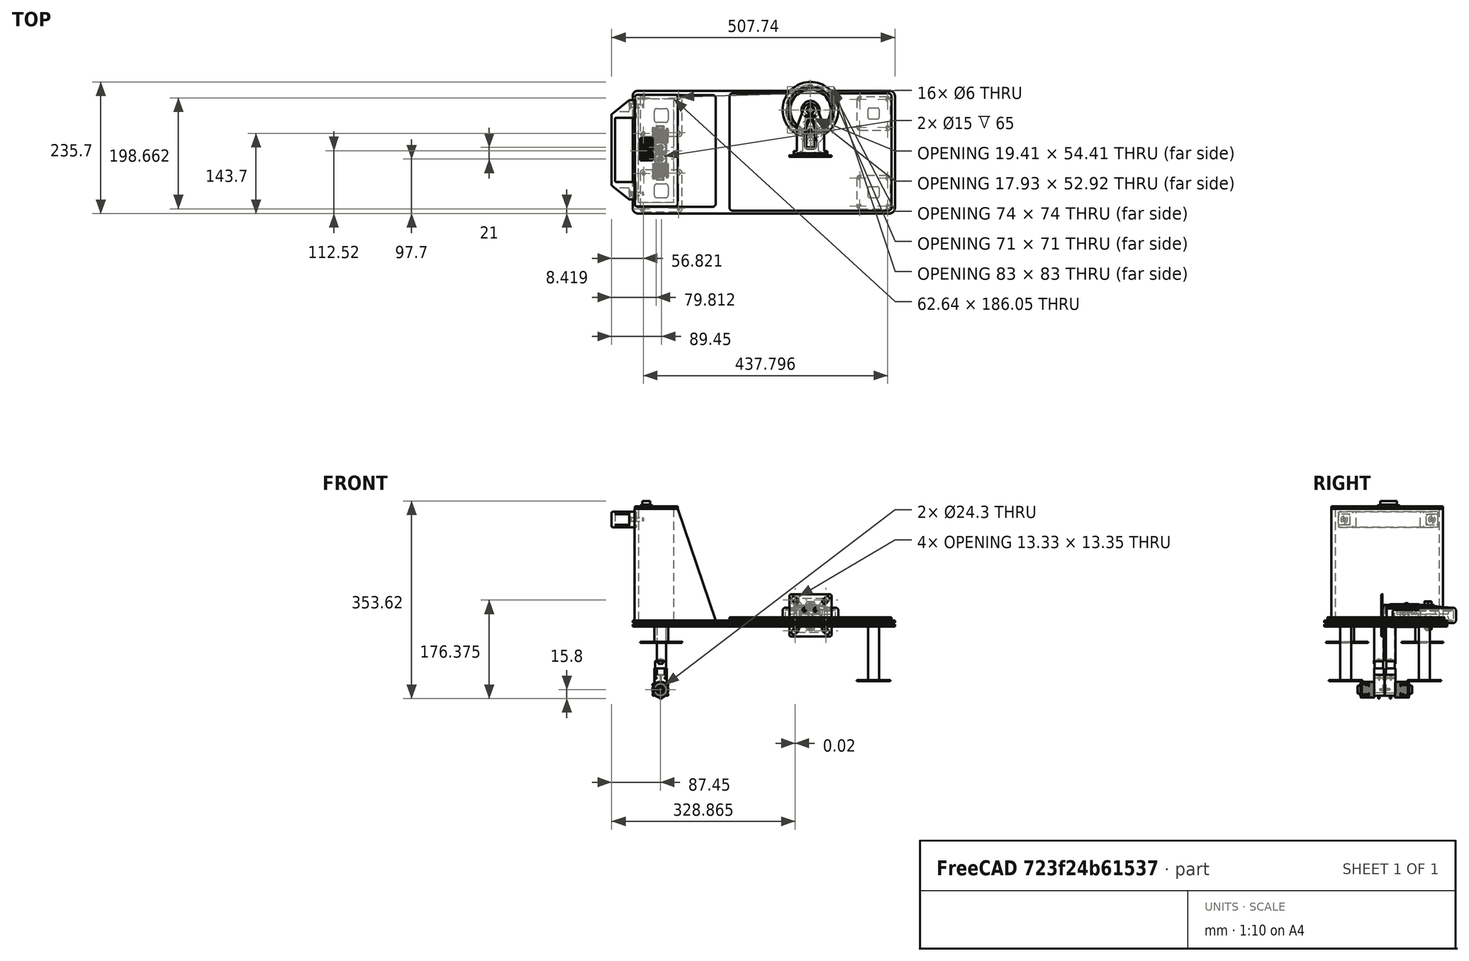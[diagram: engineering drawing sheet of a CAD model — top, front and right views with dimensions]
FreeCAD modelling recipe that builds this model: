
FCSTD DOCUMENT  (FreeCAD 0.19R24267 (Git))
Label: Assembly
License: All rights reserved
LicenseURL: http://en.wikipedia.org/wiki/All_rights_reserved
objects: PartDesign::Fillet×53, Part::Feature×42, Sketcher::SketchObject×24, PartDesign::Pad×15, PartDesign::Hole×12, PartDesign::Body×11, Part::Compound2×4, PartDesign::Pocket×3, Mesh::Feature×1
note: 243 computed .brp shape members not serialized (recipe doc carries the construction recipe); baked Part::Feature solids carry a one-line shape summary decoded from their .brp

FEATURE [Part::Feature] Solid004
  shape: bbox 35.72 x 35.72 x 6.7 mm, 21 faces (baked)
FEATURE [Part::Feature] Solid003
  shape: bbox 35.72 x 35.72 x 6.7 mm, 21 faces (baked)
FEATURE [Part::Feature] Solid
  shape: bbox 44.32 x 44.32 x 22 mm, 34 faces (baked)
FEATURE [Part::Feature] Solid002
  shape: bbox 8 x 8 x 23 mm, 6 faces (baked)
FEATURE [Part::Feature] Solid008
  shape: bbox 42.23 x 52 x 29.25 mm, 248 faces (baked)
FEATURE [Part::Feature] Solid001
  shape: bbox 53.41 x 53.41 x 20 mm, 10 faces (baked)
FEATURE [Part::Feature] Solid007
  shape: bbox 11.32 x 11.32 x 6 mm, 21 faces (baked)
FEATURE [Part::Feature] Solid006
  shape: bbox 12.03 x 11.6 x 41.03 mm, 57 faces (baked)
FEATURE [Part::Feature] Solid005
  shape: bbox 60 x 5.2 x 60 mm, 62 faces (baked)
FEATURE [Part::Compound2] Compound  label="Castor 50 mm (1)"
  Links = -> [Solid,Solid001,Solid002,Solid003,Solid004,Solid005,Solid006,Solid007,Solid008]
  Placement = pos=(114,75,-120) rot=(1,0,0;4.71239rad)
FEATURE [Part::Feature] Solid009
  shape: bbox 12 x 12 x 32 mm, 6 faces (baked)
FEATURE [Part::Feature] Solid010
  shape: bbox 16.34 x 16.34 x 6.924 mm, 32 faces (baked)
FEATURE [Part::Feature] Solid011
  shape: bbox 97.41 x 97.42 x 31.4 mm, 44 faces (baked)
FEATURE [Part::Feature] Solid012
  shape: bbox 77.93 x 77.93 x 5.5 mm, 23 faces (baked)
FEATURE [Part::Feature] Solid013
  shape: bbox 64.37 x 92.7 x 40.6 mm, 222 faces (baked)
FEATURE [Part::Feature] Solid014
  shape: bbox 76 x 7.5 x 76 mm, 58 faces (baked)
FEATURE [Part::Feature] Solid015
  shape: bbox 108.2 x 108.2 x 27 mm, 22 faces (baked)
FEATURE [Part::Feature] Solid016
  shape: bbox 15.51 x 14.96 x 52.39 mm, 65 faces (baked)
FEATURE [Part::Feature] Solid017
  shape: bbox 77.93 x 77.93 x 5.5 mm, 23 faces (baked)
FEATURE [Part::Compound2] Compound001  label="Castor 100 mm (1)"
  Links = -> [Solid011,Solid015,Solid009,Solid012,Solid017,Solid014,Solid016,Solid010,Solid013]
  Placement = pos=(-269,71,-51.5) rot=(0,-0.707107,0.707107;3.14159rad)
FEATURE [Part::Feature] Solid018
  shape: bbox 16.34 x 16.34 x 6.924 mm, 32 faces (baked)
FEATURE [Part::Feature] Solid019
  shape: bbox 97.41 x 97.42 x 31.4 mm, 44 faces (baked)
FEATURE [Part::Feature] Solid020
  shape: bbox 108.2 x 108.2 x 27 mm, 22 faces (baked)
FEATURE [Part::Feature] Solid021
  shape: bbox 15.51 x 14.96 x 52.39 mm, 65 faces (baked)
FEATURE [Part::Feature] Solid022
  shape: bbox 77.93 x 77.93 x 5.5 mm, 23 faces (baked)
FEATURE [Part::Feature] Solid023
  shape: bbox 76 x 7.5 x 76 mm, 58 faces (baked)
FEATURE [Part::Feature] Solid024
  shape: bbox 12 x 12 x 32 mm, 6 faces (baked)
FEATURE [Part::Feature] Solid025
  shape: bbox 64.37 x 92.7 x 40.6 mm, 222 faces (baked)
FEATURE [Part::Feature] Solid026
  shape: bbox 77.93 x 77.93 x 5.5 mm, 23 faces (baked)
FEATURE [Part::Compound2] Compound002  label="Castor 100 mm (2)"
  Links = -> [Solid019,Solid020,Solid024,Solid022,Solid026,Solid023,Solid021,Solid018,Solid025]
  Placement = pos=(-268,-63,-51.5) rot=(1,0,0;4.71239rad)
FEATURE [Part::Feature] Solid027
  shape: bbox 44.32 x 44.32 x 22 mm, 34 faces (baked)
FEATURE [Part::Feature] Solid028
  shape: bbox 35.72 x 35.72 x 6.7 mm, 21 faces (baked)
FEATURE [Part::Feature] Solid029
  shape: bbox 35.72 x 35.72 x 6.7 mm, 21 faces (baked)
FEATURE [Part::Feature] Solid030
  shape: bbox 42.23 x 52 x 29.25 mm, 248 faces (baked)
FEATURE [Part::Feature] Solid031
  shape: bbox 53.41 x 53.41 x 20 mm, 10 faces (baked)
FEATURE [Part::Feature] Solid032
  shape: bbox 8 x 8 x 23 mm, 6 faces (baked)
FEATURE [Part::Feature] Solid033
  shape: bbox 60 x 5.2 x 60 mm, 62 faces (baked)
FEATURE [Part::Feature] Solid034
  shape: bbox 11.32 x 11.32 x 6 mm, 21 faces (baked)
FEATURE [Part::Feature] Solid035
  shape: bbox 12.03 x 11.6 x 41.03 mm, 57 faces (baked)
FEATURE [Part::Compound2] Compound003  label="Castor 50 mm (2)"
  Links = -> [Solid027,Solid031,Solid032,Solid028,Solid029,Solid033,Solid035,Solid034,Solid030]
  Placement = pos=(114,-67,-118) rot=(1,0,0;4.71239rad)
FEATURE [Sketcher::SketchObject] Sketch
  FullyConstrained = false
  MapMode = 5
  Support = -> [XY_Plane]
  sketch-geometry (4):
    g0: LineSegment StartX=-121.71 StartY=116.298 StartZ=0 EndX=348.29 EndY=116.298 EndZ=0
    g1: LineSegment StartX=348.29 StartY=116.298 StartZ=0 EndX=348.29 EndY=-103.702 EndZ=0
    g2: LineSegment StartX=348.29 StartY=-103.702 StartZ=0 EndX=-121.71 EndY=-103.702 EndZ=0
    g3: LineSegment StartX=-121.71 StartY=-103.702 StartZ=0 EndX=-121.71 EndY=116.298 EndZ=0
  constraints (10):
    c: Coincident(g0,g1)
    c: Coincident(g1,g2)
    c: Coincident(g2,g3)
    c: Coincident(g3,g0)
    c: Horizontal(g0)
    c: Horizontal(g2)
    c: Vertical(g1)
    c: Vertical(g3)
    c: DistanceY(g1,g1) = 220
    c: DistanceX(g2,g2) = 470
FEATURE [PartDesign::Pad] Pad
  Direction = (1,1,1)
  Length = 4
  Length2 = 100
  Profile = -> Sketch
  Type = 0
FEATURE [PartDesign::Fillet] Fillet
  Base = -> Pad [Edge5]
  BaseFeature = -> Pad
  Radius = 10
  SupportTransform = false
FEATURE [PartDesign::Fillet] Fillet001
  Base = -> Fillet [Edge3]
  BaseFeature = -> Fillet
  Radius = 10
  SupportTransform = false
FEATURE [PartDesign::Fillet] Fillet002
  Base = -> Fillet001 [Edge18]
  BaseFeature = -> Fillet001
  Radius = 10
  SupportTransform = false
FEATURE [PartDesign::Fillet] Fillet003
  Base = -> Fillet002 [Edge15]
  BaseFeature = -> Fillet002
  Radius = 10
  SupportTransform = false
FEATURE [PartDesign::Body] Body  label="Base plate 1"
  Group = -> [Sketch,Pad,Fillet,Fillet001,Fillet002,Fillet003]
  Origin = -> Origin
  Placement = pos=(-197,-0.5,-13) rot=(0,0,1;0rad)
  Tip = -> Fillet003
FEATURE [Sketcher::SketchObject] Sketch001
  FullyConstrained = false
  MapMode = 5
  Support = -> [XY_Plane001]
  sketch-geometry (4):
    g0: LineSegment StartX=-121.71 StartY=116.298 StartZ=0 EndX=348.29 EndY=116.298 EndZ=0
    g1: LineSegment StartX=348.29 StartY=116.298 StartZ=0 EndX=348.29 EndY=-103.702 EndZ=0
    g2: LineSegment StartX=348.29 StartY=-103.702 StartZ=0 EndX=-121.71 EndY=-103.702 EndZ=0
    g3: LineSegment StartX=-121.71 StartY=-103.702 StartZ=0 EndX=-121.71 EndY=116.298 EndZ=0
  constraints (10):
    c: Coincident(g0,g1)
    c: Coincident(g1,g2)
    c: Coincident(g2,g3)
    c: Coincident(g3,g0)
    c: Horizontal(g0)
    c: Horizontal(g2)
    c: Vertical(g1)
    c: Vertical(g3)
    c: DistanceY(g1,g1) = 220
    c: DistanceX(g2,g2) = 470
FEATURE [PartDesign::Pad] Pad001
  Direction = (1,1,1)
  Length = 4
  Length2 = 100
  Profile = -> Sketch001
  Type = 0
FEATURE [PartDesign::Fillet] Fillet006
  Base = -> Pad001 [Edge5]
  BaseFeature = -> Pad001
  Radius = 10
  SupportTransform = false
FEATURE [PartDesign::Fillet] Fillet004
  Base = -> Fillet006 [Edge3]
  BaseFeature = -> Fillet006
  Radius = 10
  SupportTransform = false
FEATURE [PartDesign::Fillet] Fillet005
  Base = -> Fillet004 [Edge18]
  BaseFeature = -> Fillet004
  Radius = 10
  SupportTransform = false
FEATURE [PartDesign::Fillet] Fillet007
  Base = -> Fillet005 [Edge15]
  BaseFeature = -> Fillet005
  Radius = 10
  SupportTransform = false
FEATURE [PartDesign::Body] Body001  label="Base plate 2"
  Group = -> [Sketch001,Pad001,Fillet006,Fillet004,Fillet005,Fillet007]
  Origin = -> Origin001
  Placement = pos=(-197,-0.5,-20) rot=(0,0,1;0rad)
  Tip = -> Fillet007
FEATURE [Sketcher::SketchObject] Sketch004
  FullyConstrained = true
  MapMode = 5
  Support = -> [XY_Plane002]
  sketch-geometry (4):
    g0: LineSegment StartX=0 StartY=0 StartZ=0 EndX=20 EndY=0 EndZ=0
    g1: LineSegment StartX=20 StartY=0 StartZ=0 EndX=20 EndY=-20 EndZ=0
    g2: LineSegment StartX=20 StartY=-20 StartZ=0 EndX=0 EndY=-20 EndZ=0
    g3: LineSegment StartX=0 StartY=-20 StartZ=0 EndX=0 EndY=0 EndZ=0
  constraints (11):
    c: Coincident(g0,g1)
    c: Coincident(g1,g2)
    c: Coincident(g2,g3)
    c: Coincident(g3,g0)
    c: Horizontal(g0)
    c: Horizontal(g2)
    c: Vertical(g1)
    c: Vertical(g3)
    c: Coincident(g0,g-1)
    c: DistanceX(g0,g0) = 20
    c: DistanceY(g1,g1) = 20
FEATURE [PartDesign::Pad] Pad002
  Direction = (1,1,1)
  Length = 100
  Length2 = 100
  Profile = -> Sketch004
  Type = 0
FEATURE [PartDesign::Fillet] Fillet010
  Base = -> Pad002 [Edge8,Edge2,Edge1]
  BaseFeature = -> Pad002
  Radius = 3
  SupportTransform = false
FEATURE [PartDesign::Fillet] Fillet011
  Base = -> Fillet010 [Edge20]
  BaseFeature = -> Fillet010
  Radius = 3
  SupportTransform = false
FEATURE [Sketcher::SketchObject] Sketch003
  FullyConstrained = true
  MapMode = 5
  Placement = pos=(0,0,0) rot=(1,0,0;3.14159rad)
  Support = -> [Fillet011]
  sketch-geometry (4):
    g0: LineSegment StartX=-20 StartY=40 StartZ=0 EndX=40 EndY=40 EndZ=0
    g1: LineSegment StartX=40 StartY=40 StartZ=0 EndX=40 EndY=-20 EndZ=0
    g2: LineSegment StartX=40 StartY=-20 StartZ=0 EndX=-20 EndY=-20 EndZ=0
    g3: LineSegment StartX=-20 StartY=-20 StartZ=0 EndX=-20 EndY=40 EndZ=0
  constraints (12):
    c: Coincident(g0,g1)
    c: Coincident(g1,g2)
    c: Coincident(g2,g3)
    c: Coincident(g3,g0)
    c: Horizontal(g0)
    c: Horizontal(g2)
    c: Vertical(g1)
    c: Vertical(g3)
    c: DistanceX(g2,g2) = 60
    c: DistanceY(g1,g1) = 60
    c: DistanceY(g-1,g0) = 40
    c: DistanceX(g0,g-1) = 20
FEATURE [PartDesign::Pad] Pad003
  BaseFeature = -> Fillet011
  Direction = (1,1,1)
  Length = 2
  Length2 = 95
  Profile = -> Sketch003
  Type = 0
FEATURE [PartDesign::Fillet] Fillet013
  Base = -> Pad003 [Edge5]
  BaseFeature = -> Pad003
  Radius = 5
  SupportTransform = false
FEATURE [PartDesign::Fillet] Fillet009
  Base = -> Fillet013 [Edge23]
  BaseFeature = -> Fillet013
  Radius = 5
  SupportTransform = false
FEATURE [PartDesign::Fillet] Fillet008
  Base = -> Fillet009 [Edge24]
  BaseFeature = -> Fillet009
  Radius = 5
  SupportTransform = false
FEATURE [PartDesign::Fillet] Fillet012
  Base = -> Fillet008 [Edge23]
  BaseFeature = -> Fillet008
  Radius = 5
  SupportTransform = false
FEATURE [Sketcher::SketchObject] Sketch002
  FullyConstrained = false
  MapMode = 5
  Placement = pos=(0,0,-2) rot=(1,0,0;3.14159rad)
  Support = -> [Fillet012]
  sketch-geometry (4):
    g0: Circle CenterX=-14.6652 CenterY=-15.2975 CenterZ=0 NormalX=0 NormalY=0 NormalZ=1 AngleXU=0 Radius=3
    g1: Circle CenterX=35.0398 CenterY=-15.0446 CenterZ=0 NormalX=0 NormalY=0 NormalZ=1 AngleXU=0 Radius=3
    g2: Circle CenterX=35.1663 CenterY=35.1663 CenterZ=0 NormalX=0 NormalY=0 NormalZ=1 AngleXU=0 Radius=3
    g3: Circle CenterX=-15.0446 CenterY=34.7869 CenterZ=0 NormalX=0 NormalY=0 NormalZ=1 AngleXU=0 Radius=3
  constraints (4):
    c: Radius(g2) = 3
    c: Radius(g3) = 3
    c: Radius(g0) = 3
    c: Radius(g1) = 3
FEATURE [PartDesign::Hole] Hole
  BaseFeature = -> Fillet012
  Depth = 25
  DepthType = 0
  Diameter = 6
  DrillForDepth = false
  DrillPoint = 1
  DrillPointAngle = 118
  HoleCutCountersinkAngle = 90
  HoleCutCustomValues = false
  HoleCutDepth = 0
  HoleCutDiameter = 6.1
  HoleCutType = 0
  ModelActualThread = false
  Profile = -> Sketch002
  Tapered = false
  TaperedAngle = 90
  ThreadAngle = 0
  ThreadClass = 0
  ThreadCutOffInner = 0
  ThreadCutOffOuter = 0
  ThreadDirection = 0
  ThreadFit = 0
  ThreadPitch = 0
  ThreadSize = 0
  ThreadType = 0
  Threaded = false
FEATURE [PartDesign::Body] Body002  label="Front Wheel Support 1"
  Group = -> [Sketch004,Pad002,Fillet010,Fillet011,Sketch003,Pad003,Fillet013,Fillet009,Fillet008,Fillet012,Sketch002,Hole]
  Origin = -> Origin002
  Placement = pos=(103,85,-116) rot=(0,0,1;0rad)
  Tip = -> Hole
FEATURE [Sketcher::SketchObject] Sketch007
  FullyConstrained = true
  MapMode = 5
  Support = -> [XY_Plane003]
  sketch-geometry (4):
    g0: LineSegment StartX=0 StartY=0 StartZ=0 EndX=20 EndY=0 EndZ=0
    g1: LineSegment StartX=20 StartY=0 StartZ=0 EndX=20 EndY=-20 EndZ=0
    g2: LineSegment StartX=20 StartY=-20 StartZ=0 EndX=0 EndY=-20 EndZ=0
    g3: LineSegment StartX=0 StartY=-20 StartZ=0 EndX=0 EndY=0 EndZ=0
  constraints (11):
    c: Coincident(g0,g1)
    c: Coincident(g1,g2)
    c: Coincident(g2,g3)
    c: Coincident(g3,g0)
    c: Horizontal(g0)
    c: Horizontal(g2)
    c: Vertical(g1)
    c: Vertical(g3)
    c: Coincident(g0,g-1)
    c: DistanceX(g0,g0) = 20
    c: DistanceY(g1,g1) = 20
FEATURE [PartDesign::Pad] Pad004
  Direction = (1,1,1)
  Length = 100
  Length2 = 100
  Profile = -> Sketch007
  Type = 0
FEATURE [PartDesign::Fillet] Fillet016
  Base = -> Pad004 [Edge8,Edge2,Edge1]
  BaseFeature = -> Pad004
  Radius = 3
  SupportTransform = false
FEATURE [PartDesign::Fillet] Fillet017
  Base = -> Fillet016 [Edge20]
  BaseFeature = -> Fillet016
  Radius = 3
  SupportTransform = false
FEATURE [Sketcher::SketchObject] Sketch006
  FullyConstrained = true
  MapMode = 5
  Placement = pos=(0,0,0) rot=(1,0,0;3.14159rad)
  Support = -> [Fillet017]
  sketch-geometry (4):
    g0: LineSegment StartX=-20 StartY=40 StartZ=0 EndX=40 EndY=40 EndZ=0
    g1: LineSegment StartX=40 StartY=40 StartZ=0 EndX=40 EndY=-20 EndZ=0
    g2: LineSegment StartX=40 StartY=-20 StartZ=0 EndX=-20 EndY=-20 EndZ=0
    g3: LineSegment StartX=-20 StartY=-20 StartZ=0 EndX=-20 EndY=40 EndZ=0
  constraints (12):
    c: Coincident(g0,g1)
    c: Coincident(g1,g2)
    c: Coincident(g2,g3)
    c: Coincident(g3,g0)
    c: Horizontal(g0)
    c: Horizontal(g2)
    c: Vertical(g1)
    c: Vertical(g3)
    c: DistanceX(g2,g2) = 60
    c: DistanceY(g1,g1) = 60
    c: DistanceY(g-1,g0) = 40
    c: DistanceX(g0,g-1) = 20
FEATURE [PartDesign::Pad] Pad005
  BaseFeature = -> Fillet017
  Direction = (1,1,1)
  Length = 2
  Length2 = 95
  Profile = -> Sketch006
  Type = 0
FEATURE [PartDesign::Fillet] Fillet019
  Base = -> Pad005 [Edge5]
  BaseFeature = -> Pad005
  Radius = 5
  SupportTransform = false
FEATURE [PartDesign::Fillet] Fillet015
  Base = -> Fillet019 [Edge23]
  BaseFeature = -> Fillet019
  Radius = 5
  SupportTransform = false
FEATURE [PartDesign::Fillet] Fillet014
  Base = -> Fillet015 [Edge24]
  BaseFeature = -> Fillet015
  Radius = 5
  SupportTransform = false
FEATURE [PartDesign::Fillet] Fillet018
  Base = -> Fillet014 [Edge23]
  BaseFeature = -> Fillet014
  Radius = 5
  SupportTransform = false
FEATURE [Sketcher::SketchObject] Sketch005
  FullyConstrained = false
  MapMode = 5
  Placement = pos=(0,0,-2) rot=(1,0,0;3.14159rad)
  Support = -> [Fillet018]
  sketch-geometry (4):
    g0: Circle CenterX=-14.6652 CenterY=-15.2975 CenterZ=0 NormalX=0 NormalY=0 NormalZ=1 AngleXU=0 Radius=3
    g1: Circle CenterX=35.0398 CenterY=-15.0446 CenterZ=0 NormalX=0 NormalY=0 NormalZ=1 AngleXU=0 Radius=3
    g2: Circle CenterX=35.1663 CenterY=35.1663 CenterZ=0 NormalX=0 NormalY=0 NormalZ=1 AngleXU=0 Radius=3
    g3: Circle CenterX=-15.0446 CenterY=34.7869 CenterZ=0 NormalX=0 NormalY=0 NormalZ=1 AngleXU=0 Radius=3
  constraints (4):
    c: Radius(g2) = 3
    c: Radius(g3) = 3
    c: Radius(g0) = 3
    c: Radius(g1) = 3
FEATURE [PartDesign::Hole] Hole001
  BaseFeature = -> Fillet018
  Depth = 25
  DepthType = 0
  Diameter = 6
  DrillForDepth = false
  DrillPoint = 1
  DrillPointAngle = 118
  HoleCutCountersinkAngle = 90
  HoleCutCustomValues = false
  HoleCutDepth = 0
  HoleCutDiameter = 6.1
  HoleCutType = 0
  ModelActualThread = false
  Profile = -> Sketch005
  Tapered = false
  TaperedAngle = 90
  ThreadAngle = 0
  ThreadClass = 0
  ThreadCutOffInner = 0
  ThreadCutOffOuter = 0
  ThreadDirection = 0
  ThreadFit = 0
  ThreadPitch = 0
  ThreadSize = 0
  ThreadType = 0
  Threaded = false
FEATURE [PartDesign::Body] Body003  label="Front Wheel Support 2"
  Group = -> [Sketch007,Pad004,Fillet016,Fillet017,Sketch006,Pad005,Fillet019,Fillet015,Fillet014,Fillet018,Sketch005,Hole001]
  Origin = -> Origin003
  Placement = pos=(103,-56,-116) rot=(0,0,1;0rad)
  Tip = -> Hole001
FEATURE [Sketcher::SketchObject] Sketch009
  FullyConstrained = true
  MapMode = 5
  Support = -> [XY_Plane004]
  sketch-geometry (4):
    g0: LineSegment StartX=0 StartY=0 StartZ=0 EndX=75 EndY=0 EndZ=0
    g1: LineSegment StartX=75 StartY=0 StartZ=0 EndX=75 EndY=-75 EndZ=0
    g2: LineSegment StartX=75 StartY=-75 StartZ=0 EndX=0 EndY=-75 EndZ=0
    g3: LineSegment StartX=0 StartY=-75 StartZ=0 EndX=0 EndY=0 EndZ=0
  constraints (11):
    c: Coincident(g0,g1)
    c: Coincident(g1,g2)
    c: Coincident(g2,g3)
    c: Coincident(g3,g0)
    c: Horizontal(g0)
    c: Horizontal(g2)
    c: Vertical(g1)
    c: Vertical(g3)
    c: Coincident(g0,g-1)
    c: DistanceX(g0,g0) = 75
    c: DistanceY(g1,g1) = 75
FEATURE [PartDesign::Pad] Pad006
  Direction = (1,1,1)
  Length = 2
  Length2 = 100
  Profile = -> Sketch009
  Type = 0
FEATURE [PartDesign::Fillet] Fillet020
  Base = -> Pad006 [Edge5]
  BaseFeature = -> Pad006
  Radius = 5
  SupportTransform = false
FEATURE [PartDesign::Fillet] Fillet021
  Base = -> Fillet020 [Edge15]
  BaseFeature = -> Fillet020
  Radius = 5
  SupportTransform = false
FEATURE [PartDesign::Fillet] Fillet022
  Base = -> Fillet021 [Edge16]
  BaseFeature = -> Fillet021
  Radius = 5
  SupportTransform = false
FEATURE [PartDesign::Fillet] Fillet023
  Base = -> Fillet022 [Edge15]
  BaseFeature = -> Fillet022
  Radius = 5
  SupportTransform = false
FEATURE [Sketcher::SketchObject] Sketch010
  FullyConstrained = true
  MapMode = 5
  Support = -> [XY_Plane004]
FEATURE [Sketcher::SketchObject] Sketch011
  FullyConstrained = false
  MapMode = 5
  Support = -> [XY_Plane004]
  sketch-geometry (4):
    g0: Circle CenterX=5.3706 CenterY=-5.21873 CenterZ=0 NormalX=0 NormalY=0 NormalZ=1 AngleXU=0 Radius=3
    g1: Circle CenterX=6.00298 CenterY=-68.7095 CenterZ=0 NormalX=0 NormalY=0 NormalZ=1 AngleXU=0 Radius=3
    g2: Circle CenterX=68.7895 CenterY=-68.8809 CenterZ=0 NormalX=0 NormalY=0 NormalZ=1 AngleXU=0 Radius=3
    g3: Circle CenterX=68.7895 CenterY=-6.40196 CenterZ=0 NormalX=0 NormalY=0 NormalZ=1 AngleXU=0 Radius=3
  constraints (4):
    c: Radius(g1) = 3
    c: Radius(g0) = 3
    c: Radius(g3) = 3
    c: Radius(g2) = 3
FEATURE [PartDesign::Hole] Hole005
  BaseFeature = -> Fillet023
  Depth = 25
  DepthType = 0
  Diameter = 6
  DrillForDepth = false
  DrillPoint = 1
  DrillPointAngle = 118
  HoleCutCountersinkAngle = 90
  HoleCutCustomValues = false
  HoleCutDepth = 0
  HoleCutDiameter = 6.1
  HoleCutType = 0
  ModelActualThread = false
  Profile = -> Sketch011
  Tapered = false
  TaperedAngle = 90
  ThreadAngle = 0
  ThreadClass = 0
  ThreadCutOffInner = 0
  ThreadCutOffOuter = 0
  ThreadDirection = 0
  ThreadFit = 0
  ThreadPitch = 0
  ThreadSize = 0
  ThreadType = 0
  Threaded = false
FEATURE [PartDesign::Hole] Hole006
  BaseFeature = -> Hole005
  Depth = 25
  DepthType = 0
  Diameter = 6
  DrillForDepth = false
  DrillPoint = 1
  DrillPointAngle = 118
  HoleCutCountersinkAngle = 90
  HoleCutCustomValues = false
  HoleCutDepth = 0
  HoleCutDiameter = 6.1
  HoleCutType = 0
  ModelActualThread = false
  Profile = -> Hole005 [Face4]
  Tapered = false
  TaperedAngle = 90
  ThreadAngle = 0
  ThreadClass = 0
  ThreadCutOffInner = 0
  ThreadCutOffOuter = 0
  ThreadDirection = 0
  ThreadFit = 0
  ThreadPitch = 0
  ThreadSize = 0
  ThreadType = 0
  Threaded = false
FEATURE [PartDesign::Hole] Hole002
  BaseFeature = -> Hole006
  Depth = 25
  DepthType = 0
  Diameter = 6
  DrillForDepth = false
  DrillPoint = 1
  DrillPointAngle = 118
  HoleCutCountersinkAngle = 90
  HoleCutCustomValues = false
  HoleCutDepth = 0
  HoleCutDiameter = 6.1
  HoleCutType = 0
  ModelActualThread = false
  Profile = -> Hole006 [Face13]
  Tapered = false
  TaperedAngle = 90
  ThreadAngle = 0
  ThreadClass = 0
  ThreadCutOffInner = 0
  ThreadCutOffOuter = 0
  ThreadDirection = 0
  ThreadFit = 0
  ThreadPitch = 0
  ThreadSize = 0
  ThreadType = 0
  Threaded = false
FEATURE [PartDesign::Hole] Hole003
  BaseFeature = -> Hole002
  Depth = 25
  DepthType = 0
  Diameter = 6
  DrillForDepth = false
  DrillPoint = 1
  DrillPointAngle = 118
  HoleCutCountersinkAngle = 90
  HoleCutCustomValues = false
  HoleCutDepth = 0
  HoleCutDiameter = 6.1
  HoleCutType = 0
  ModelActualThread = false
  Profile = -> Hole002 [Face10]
  Tapered = false
  TaperedAngle = 90
  ThreadAngle = 0
  ThreadClass = 0
  ThreadCutOffInner = 0
  ThreadCutOffOuter = 0
  ThreadDirection = 0
  ThreadFit = 0
  ThreadPitch = 0
  ThreadSize = 0
  ThreadType = 0
  Threaded = false
FEATURE [PartDesign::Hole] Hole004
  BaseFeature = -> Hole003
  Depth = 25
  DepthType = 0
  Diameter = 6
  DrillForDepth = false
  DrillPoint = 1
  DrillPointAngle = 118
  HoleCutCountersinkAngle = 90
  HoleCutCustomValues = false
  HoleCutDepth = 0
  HoleCutDiameter = 6.1
  HoleCutType = 0
  ModelActualThread = false
  Profile = -> Hole003 [Face11]
  Tapered = false
  TaperedAngle = 90
  ThreadAngle = 0
  ThreadClass = 0
  ThreadCutOffInner = 0
  ThreadCutOffOuter = 0
  ThreadDirection = 0
  ThreadFit = 0
  ThreadPitch = 0
  ThreadSize = 0
  ThreadType = 0
  Threaded = false
FEATURE [Sketcher::SketchObject] Sketch008
  FullyConstrained = true
  MapMode = 5
  Placement = pos=(0,0,0) rot=(1,0,0;3.14159rad)
  Support = -> [Hole004]
  sketch-geometry (4):
    g0: LineSegment StartX=25 StartY=50 StartZ=0 EndX=50 EndY=50 EndZ=0
    g1: LineSegment StartX=50 StartY=50 StartZ=0 EndX=50 EndY=25 EndZ=0
    g2: LineSegment StartX=50 StartY=25 StartZ=0 EndX=25 EndY=25 EndZ=0
    g3: LineSegment StartX=25 StartY=25 StartZ=0 EndX=25 EndY=50 EndZ=0
  constraints (12):
    c: Coincident(g0,g1)
    c: Coincident(g1,g2)
    c: Coincident(g2,g3)
    c: Coincident(g3,g0)
    c: Horizontal(g0)
    c: Horizontal(g2)
    c: Vertical(g1)
    c: Vertical(g3)
    c: DistanceY(g1,g1) = 25
    c: DistanceX(g2,g2) = 25
    c: DistanceY(g-1,g2) = 25
    c: DistanceX(g-1,g2) = 25
FEATURE [PartDesign::Pad] Pad007
  BaseFeature = -> Hole004
  Direction = (1,1,1)
  Length = 29
  Length2 = 100
  Profile = -> Sketch008
  Type = 0
FEATURE [Sketcher::SketchObject] Sketch013
  FullyConstrained = true
  MapMode = 5
  Support = -> [XY_Plane005]
  sketch-geometry (4):
    g0: LineSegment StartX=0 StartY=0 StartZ=0 EndX=75 EndY=0 EndZ=0
    g1: LineSegment StartX=75 StartY=0 StartZ=0 EndX=75 EndY=-75 EndZ=0
    g2: LineSegment StartX=75 StartY=-75 StartZ=0 EndX=0 EndY=-75 EndZ=0
    g3: LineSegment StartX=0 StartY=-75 StartZ=0 EndX=0 EndY=0 EndZ=0
  constraints (11):
    c: Coincident(g0,g1)
    c: Coincident(g1,g2)
    c: Coincident(g2,g3)
    c: Coincident(g3,g0)
    c: Horizontal(g0)
    c: Horizontal(g2)
    c: Vertical(g1)
    c: Vertical(g3)
    c: Coincident(g0,g-1)
    c: DistanceX(g0,g0) = 75
    c: DistanceY(g1,g1) = 75
FEATURE [PartDesign::Pad] Pad008
  Direction = (1,1,1)
  Length = 2
  Length2 = 100
  Profile = -> Sketch013
  Type = 0
FEATURE [PartDesign::Fillet] Fillet024
  Base = -> Pad008 [Edge5]
  BaseFeature = -> Pad008
  Radius = 5
  SupportTransform = false
FEATURE [PartDesign::Fillet] Fillet025
  Base = -> Fillet024 [Edge15]
  BaseFeature = -> Fillet024
  Radius = 5
  SupportTransform = false
FEATURE [PartDesign::Fillet] Fillet026
  Base = -> Fillet025 [Edge16]
  BaseFeature = -> Fillet025
  Radius = 5
  SupportTransform = false
FEATURE [PartDesign::Fillet] Fillet027
  Base = -> Fillet026 [Edge15]
  BaseFeature = -> Fillet026
  Radius = 5
  SupportTransform = false
FEATURE [Sketcher::SketchObject] Sketch014
  FullyConstrained = true
  MapMode = 5
  Support = -> [XY_Plane005]
FEATURE [Sketcher::SketchObject] Sketch015
  FullyConstrained = false
  MapMode = 5
  Support = -> [XY_Plane005]
  sketch-geometry (4):
    g0: Circle CenterX=5.3706 CenterY=-5.21873 CenterZ=0 NormalX=0 NormalY=0 NormalZ=1 AngleXU=0 Radius=3
    g1: Circle CenterX=6.00298 CenterY=-68.7095 CenterZ=0 NormalX=0 NormalY=0 NormalZ=1 AngleXU=0 Radius=3
    g2: Circle CenterX=68.7895 CenterY=-68.8809 CenterZ=0 NormalX=0 NormalY=0 NormalZ=1 AngleXU=0 Radius=3
    g3: Circle CenterX=68.7895 CenterY=-6.40196 CenterZ=0 NormalX=0 NormalY=0 NormalZ=1 AngleXU=0 Radius=3
  constraints (4):
    c: Radius(g1) = 3
    c: Radius(g0) = 3
    c: Radius(g3) = 3
    c: Radius(g2) = 3
FEATURE [PartDesign::Hole] Hole009
  BaseFeature = -> Fillet027
  Depth = 25
  DepthType = 0
  Diameter = 6
  DrillForDepth = false
  DrillPoint = 1
  DrillPointAngle = 118
  HoleCutCountersinkAngle = 90
  HoleCutCustomValues = false
  HoleCutDepth = 0
  HoleCutDiameter = 6.1
  HoleCutType = 0
  ModelActualThread = false
  Profile = -> Sketch015
  Tapered = false
  TaperedAngle = 90
  ThreadAngle = 0
  ThreadClass = 0
  ThreadCutOffInner = 0
  ThreadCutOffOuter = 0
  ThreadDirection = 0
  ThreadFit = 0
  ThreadPitch = 0
  ThreadSize = 0
  ThreadType = 0
  Threaded = false
FEATURE [PartDesign::Hole] Hole011
  BaseFeature = -> Hole009
  Depth = 25
  DepthType = 0
  Diameter = 6
  DrillForDepth = false
  DrillPoint = 1
  DrillPointAngle = 118
  HoleCutCountersinkAngle = 90
  HoleCutCustomValues = false
  HoleCutDepth = 0
  HoleCutDiameter = 6.1
  HoleCutType = 0
  ModelActualThread = false
  Profile = -> Hole009 [Face4]
  Tapered = false
  TaperedAngle = 90
  ThreadAngle = 0
  ThreadClass = 0
  ThreadCutOffInner = 0
  ThreadCutOffOuter = 0
  ThreadDirection = 0
  ThreadFit = 0
  ThreadPitch = 0
  ThreadSize = 0
  ThreadType = 0
  Threaded = false
FEATURE [PartDesign::Hole] Hole010
  BaseFeature = -> Hole011
  Depth = 25
  DepthType = 0
  Diameter = 6
  DrillForDepth = false
  DrillPoint = 1
  DrillPointAngle = 118
  HoleCutCountersinkAngle = 90
  HoleCutCustomValues = false
  HoleCutDepth = 0
  HoleCutDiameter = 6.1
  HoleCutType = 0
  ModelActualThread = false
  Profile = -> Hole011 [Face13]
  Tapered = false
  TaperedAngle = 90
  ThreadAngle = 0
  ThreadClass = 0
  ThreadCutOffInner = 0
  ThreadCutOffOuter = 0
  ThreadDirection = 0
  ThreadFit = 0
  ThreadPitch = 0
  ThreadSize = 0
  ThreadType = 0
  Threaded = false
FEATURE [PartDesign::Hole] Hole008
  BaseFeature = -> Hole010
  Depth = 25
  DepthType = 0
  Diameter = 6
  DrillForDepth = false
  DrillPoint = 1
  DrillPointAngle = 118
  HoleCutCountersinkAngle = 90
  HoleCutCustomValues = false
  HoleCutDepth = 0
  HoleCutDiameter = 6.1
  HoleCutType = 0
  ModelActualThread = false
  Profile = -> Hole010 [Face10]
  Tapered = false
  TaperedAngle = 90
  ThreadAngle = 0
  ThreadClass = 0
  ThreadCutOffInner = 0
  ThreadCutOffOuter = 0
  ThreadDirection = 0
  ThreadFit = 0
  ThreadPitch = 0
  ThreadSize = 0
  ThreadType = 0
  Threaded = false
FEATURE [PartDesign::Hole] Hole007
  BaseFeature = -> Hole008
  Depth = 25
  DepthType = 0
  Diameter = 6
  DrillForDepth = false
  DrillPoint = 1
  DrillPointAngle = 118
  HoleCutCountersinkAngle = 90
  HoleCutCustomValues = false
  HoleCutDepth = 0
  HoleCutDiameter = 6.1
  HoleCutType = 0
  ModelActualThread = false
  Profile = -> Hole008 [Face11]
  Tapered = false
  TaperedAngle = 90
  ThreadAngle = 0
  ThreadClass = 0
  ThreadCutOffInner = 0
  ThreadCutOffOuter = 0
  ThreadDirection = 0
  ThreadFit = 0
  ThreadPitch = 0
  ThreadSize = 0
  ThreadType = 0
  Threaded = false
FEATURE [Sketcher::SketchObject] Sketch012
  FullyConstrained = true
  MapMode = 5
  Placement = pos=(0,0,0) rot=(1,0,0;3.14159rad)
  Support = -> [Hole007]
  sketch-geometry (4):
    g0: LineSegment StartX=25 StartY=50 StartZ=0 EndX=50 EndY=50 EndZ=0
    g1: LineSegment StartX=50 StartY=50 StartZ=0 EndX=50 EndY=25 EndZ=0
    g2: LineSegment StartX=50 StartY=25 StartZ=0 EndX=25 EndY=25 EndZ=0
    g3: LineSegment StartX=25 StartY=25 StartZ=0 EndX=25 EndY=50 EndZ=0
  constraints (12):
    c: Coincident(g0,g1)
    c: Coincident(g1,g2)
    c: Coincident(g2,g3)
    c: Coincident(g3,g0)
    c: Horizontal(g0)
    c: Horizontal(g2)
    c: Vertical(g1)
    c: Vertical(g3)
    c: DistanceY(g1,g1) = 25
    c: DistanceX(g2,g2) = 25
    c: DistanceY(g-1,g2) = 25
    c: DistanceX(g-1,g2) = 25
FEATURE [PartDesign::Pad] Pad009
  BaseFeature = -> Hole007
  Direction = (1,1,1)
  Length = 29
  Length2 = 100
  Profile = -> Sketch012
  Type = 0
FEATURE [PartDesign::Fillet] Fillet028
  Base = -> Pad007 [Edge40,Edge39,Edge44]
  BaseFeature = -> Pad007
  Radius = 5
  SupportTransform = false
FEATURE [PartDesign::Fillet] Fillet029
  Base = -> Fillet028 [Edge31]
  BaseFeature = -> Fillet028
  Radius = 5
  SupportTransform = false
FEATURE [PartDesign::Body] Body004  label="Rear Wheel Support 1"
  Group = -> [Sketch009,Pad006,Fillet020,Fillet021,Fillet022,Fillet023,Sketch010,Sketch011,Hole005,Hole006,Hole002,Hole003,Hole004,Sketch008,Pad007,Fillet028,Fillet029]
  Origin = -> Origin004
  Placement = pos=(-305,-101,-47) rot=(1,0,0;3.14159rad)
  Tip = -> Fillet029
FEATURE [PartDesign::Fillet] Fillet030
  Base = -> Pad009 [Edge39]
  BaseFeature = -> Pad009
  Radius = 5
  SupportTransform = false
FEATURE [PartDesign::Fillet] Fillet031
  Base = -> Fillet030 [Edge29]
  BaseFeature = -> Fillet030
  Radius = 5
  SupportTransform = false
FEATURE [PartDesign::Fillet] Fillet032
  Base = -> Fillet031 [Edge30]
  BaseFeature = -> Fillet031
  Radius = 5
  SupportTransform = false
FEATURE [PartDesign::Fillet] Fillet033
  Base = -> Fillet032 [Edge31]
  BaseFeature = -> Fillet032
  Radius = 5
  SupportTransform = false
FEATURE [PartDesign::Body] Body005  label="Rear Wheel Support 2"
  Group = -> [Sketch013,Pad008,Fillet024,Fillet025,Fillet026,Fillet027,Sketch014,Sketch015,Hole009,Hole011,Hole010,Hole008,Hole007,Sketch012,Pad009,Fillet030,Fillet031,Fillet032,Fillet033]
  Origin = -> Origin005
  Placement = pos=(-305,34,-47) rot=(1,0,0;3.14159rad)
  Tip = -> Fillet033
FEATURE [Sketcher::SketchObject] Sketch017
  FullyConstrained = true
  MapMode = 5
  Support = -> [XY_Plane006]
  sketch-geometry (4):
    g0: LineSegment StartX=0 StartY=0 StartZ=0 EndX=145 EndY=0 EndZ=0
    g1: LineSegment StartX=145 StartY=0 StartZ=0 EndX=145 EndY=200 EndZ=0
    g2: LineSegment StartX=145 StartY=200 StartZ=0 EndX=68 EndY=200 EndZ=0
    g3: LineSegment StartX=68 StartY=200 StartZ=0 EndX=0 EndY=0 EndZ=0
  constraints (11):
    c: Coincident(g0,g-1)
    c: PointOnObject(g0,g-1)
    c: DistanceX(g0,g0) = 145
    c: Coincident(g1,g0)
    c: Vertical(g1)
    c: DistanceY(g1,g1) = 200
    c: Coincident(g2,g1)
    c: Horizontal(g2)
    c: DistanceX(g2,g2) = 77
    c: Coincident(g3,g2)
    c: Coincident(g3,g0)
FEATURE [PartDesign::Pad] Pad010
  Direction = (1,1,1)
  Length = 200
  Length2 = 100
  Profile = -> Sketch017
  Type = 0
FEATURE [PartDesign::Fillet] Fillet035
  Base = -> Pad010 [Edge11,Edge12]
  BaseFeature = -> Pad010
  Radius = 5
  SupportTransform = false
FEATURE [PartDesign::Fillet] Fillet034
  Base = -> Fillet035 [Edge14]
  BaseFeature = -> Fillet035
  Radius = 5
  SupportTransform = false
FEATURE [PartDesign::Fillet] Fillet036
  Base = -> Fillet034 [Edge15]
  BaseFeature = -> Fillet034
  Radius = 5
  SupportTransform = false
FEATURE [Sketcher::SketchObject] Sketch016
  FullyConstrained = false
  MapMode = 5
  Placement = pos=(0,200,0) rot=(0,0.707107,0.707107;3.14159rad)
  Support = -> [Fillet036]
  sketch-geometry (4):
    g0: LineSegment StartX=-137.96 StartY=193.346 StartZ=0 EndX=-75.3165 EndY=193.346 EndZ=0
    g1: LineSegment StartX=-75.3165 StartY=193.346 StartZ=0 EndX=-75.3165 EndY=7.29364 EndZ=0
    g2: LineSegment StartX=-75.3165 StartY=7.29364 StartZ=0 EndX=-137.96 EndY=7.29364 EndZ=0
    g3: LineSegment StartX=-137.96 StartY=7.29364 StartZ=0 EndX=-137.96 EndY=193.346 EndZ=0
  constraints (8):
    c: Coincident(g0,g1)
    c: Coincident(g1,g2)
    c: Coincident(g2,g3)
    c: Coincident(g3,g0)
    c: Horizontal(g0)
    c: Horizontal(g2)
    c: Vertical(g1)
    c: Vertical(g3)
FEATURE [PartDesign::Pocket] Pocket
  BaseFeature = -> Fillet036
  Length = 200
  Length2 = 100
  Profile = -> Sketch016
  Type = 0
FEATURE [PartDesign::Body] Body006  label="Instrument Box"
  Group = -> [Sketch017,Pad010,Fillet035,Fillet034,Fillet036,Sketch016,Pocket]
  Origin = -> Origin006
  Placement = pos=(-170,-92,-9) rot=(0,0.707107,0.707107;3.14159rad)
  Tip = -> Pocket
FEATURE [Sketcher::SketchObject] Sketch018
  FullyConstrained = false
  MapMode = 5
  Support = -> [XY_Plane007]
  sketch-geometry (4):
    g0: LineSegment StartX=-2.82843 StartY=104.535 StartZ=0 EndX=74.1716 EndY=104.535 EndZ=0
    g1: LineSegment StartX=74.1716 StartY=104.535 StartZ=0 EndX=74.1716 EndY=-95.4654 EndZ=0
    g2: LineSegment StartX=74.1716 StartY=-95.4654 StartZ=0 EndX=-2.82843 EndY=-95.4654 EndZ=0
    g3: LineSegment StartX=-2.82843 StartY=-95.4654 StartZ=0 EndX=-2.82843 EndY=104.535 EndZ=0
  constraints (10):
    c: Coincident(g0,g1)
    c: Coincident(g1,g2)
    c: Coincident(g2,g3)
    c: Coincident(g3,g0)
    c: Horizontal(g0)
    c: Horizontal(g2)
    c: Vertical(g1)
    c: Vertical(g3)
    c: DistanceX(g0,g0) = 77
    c: DistanceY(g1,g1) = 200
FEATURE [PartDesign::Pad] Pad011
  Direction = (1,1,1)
  Length = 4
  Length2 = 100
  Profile = -> Sketch018
  Type = 0
FEATURE [PartDesign::Fillet] Fillet038
  Base = -> Pad011 [Edge5]
  BaseFeature = -> Pad011
  Radius = 5
  SupportTransform = false
FEATURE [PartDesign::Fillet] Fillet037
  Base = -> Fillet038 [Edge15]
  BaseFeature = -> Fillet038
  Radius = 5
  SupportTransform = false
FEATURE [PartDesign::Fillet] Fillet040
  Base = -> Fillet037 [Edge14]
  BaseFeature = -> Fillet037
  Radius = 5
  SupportTransform = false
FEATURE [PartDesign::Fillet] Fillet039
  Base = -> Fillet040 [Edge15]
  BaseFeature = -> Fillet040
  Radius = 5
  SupportTransform = false
FEATURE [PartDesign::Fillet] Fillet041
  Base = -> Pad011 [Edge8]
  BaseFeature = -> Pad011
  Radius = 5
  SupportTransform = false
FEATURE [PartDesign::Fillet] Fillet042
  Base = -> Fillet041 [Edge3]
  BaseFeature = -> Fillet041
  Radius = 5
  SupportTransform = false
FEATURE [PartDesign::Fillet] Fillet043
  Base = -> Fillet042 [Edge18]
  BaseFeature = -> Fillet042
  Radius = 5
  SupportTransform = false
FEATURE [PartDesign::Fillet] Fillet044
  Base = -> Fillet043 [Edge15]
  BaseFeature = -> Fillet043
  Radius = 5
  SupportTransform = false
FEATURE [PartDesign::Body] Body007  label="Instrument Box Lid"
  Group = -> [Sketch018,Pad011,Fillet038,Fillet037,Fillet040,Fillet039,Fillet041,Fillet042,Fillet043,Fillet044]
  Origin = -> Origin007
  Placement = pos=(-312,4,191) rot=(0,0,1;0rad)
  Tip = -> Fillet044
FEATURE [Part::Feature] Feature001  label="Digital Weight Display"
  Placement = pos=(-294,11,196.5) rot=(1,0,0;1.5708rad)
  shape: bbox 22.3 x 40 x 10.9 mm, 1254 faces, 68 solids (baked)
FEATURE [Part::Feature] Feature002  label="Push Handle"
  Placement = pos=(-312,10,158) rot=(0,0,1;1.5708rad)
  shape: bbox 56.99 x 177.8 x 27.5 mm, 90 faces, 3 solids (baked)
FEATURE [Mesh::Feature] shopping_basket_1_ga001  label="Basket"
FEATURE [Sketcher::SketchObject] Sketch019
  FullyConstrained = true
  MapMode = 5
  Support = -> [XY_Plane008]
  sketch-geometry (4):
    g0: LineSegment StartX=0 StartY=0 StartZ=0 EndX=290 EndY=0 EndZ=0
    g1: LineSegment StartX=290 StartY=0 StartZ=0 EndX=290 EndY=-210 EndZ=0
    g2: LineSegment StartX=290 StartY=-210 StartZ=0 EndX=0 EndY=-210 EndZ=0
    g3: LineSegment StartX=0 StartY=-210 StartZ=0 EndX=0 EndY=0 EndZ=0
  constraints (11):
    c: Coincident(g0,g1)
    c: Coincident(g1,g2)
    c: Coincident(g2,g3)
    c: Coincident(g3,g0)
    c: Horizontal(g0)
    c: Horizontal(g2)
    c: Vertical(g1)
    c: Vertical(g3)
    c: Coincident(g0,g-1)
    c: DistanceX(g2,g2) = 290
    c: DistanceY(g1,g1) = 210
FEATURE [PartDesign::Pad] Pad012
  Direction = (1,1,1)
  Length = 3
  Length2 = 100
  Profile = -> Sketch019
  Type = 0
FEATURE [PartDesign::Fillet] Fillet045
  Base = -> Pad012 [Edge5]
  BaseFeature = -> Pad012
  Radius = 5
  SupportTransform = false
FEATURE [PartDesign::Fillet] Fillet048
  Base = -> Fillet045 [Edge15]
  BaseFeature = -> Fillet045
  Radius = 5
  SupportTransform = false
FEATURE [PartDesign::Fillet] Fillet046
  Base = -> Fillet048 [Edge14]
  BaseFeature = -> Fillet048
  Radius = 5
  SupportTransform = false
FEATURE [PartDesign::Fillet] Fillet047
  Base = -> Fillet046 [Edge15]
  BaseFeature = -> Fillet046
  Radius = 5
  SupportTransform = false
FEATURE [PartDesign::Fillet] Fillet049
  Base = -> Pad012 [Edge2]
  BaseFeature = -> Pad012
  Radius = 5
  SupportTransform = false
FEATURE [PartDesign::Fillet] Fillet050
  Base = -> Fillet049 [Edge3]
  BaseFeature = -> Fillet049
  Radius = 5
  SupportTransform = false
FEATURE [PartDesign::Fillet] Fillet051
  Base = -> Fillet050 [Edge17]
  BaseFeature = -> Fillet050
  Radius = 5
  SupportTransform = false
FEATURE [PartDesign::Fillet] Fillet052
  Base = -> Fillet051 [Edge15]
  BaseFeature = -> Fillet051
  Radius = 5
  SupportTransform = false
FEATURE [PartDesign::Body] Body008  label="Weighting Plate"
  Group = -> [Sketch019,Pad012,Fillet045,Fillet048,Fillet046,Fillet047,Fillet049,Fillet050,Fillet051,Fillet052]
  Origin = -> Origin008
  Placement = pos=(-145,111,-6.5) rot=(0,0,1;0rad)
  Tip = -> Fillet052
FEATURE [Part::Feature] Feature003  label="Shaft (1)"
  Placement = pos=(-269,-27,-133) rot=(1,0,0;1.5708rad)
  shape: bbox 30.75 x 31.11 x 30.75 mm, 1622 faces, 19 solids (baked)
FEATURE [Part::Feature] Solid036  label="Motor (1)"
  Placement = pos=(-268.5,-6.5,-116) rot=(0,1,0;3.14159rad)
  shape: bbox 22.3 x 37 x 70.8 mm, 110 faces (baked)
FEATURE [Part::Feature] Solid037  label="Motor (2)"
  Placement = pos=(-268.5,14.5,-116) rot=(1,0,0;3.14159rad)
  shape: bbox 22.3 x 37 x 70.8 mm, 110 faces (baked)
FEATURE [Part::Feature] Feature004  label="Shaft (2)"
  Placement = pos=(-269,35,-133) rot=(-1,0,0;1.5708rad)
  shape: bbox 30.75 x 31.11 x 30.75 mm, 1622 faces, 19 solids (baked)
FEATURE [Sketcher::SketchObject] Sketch020
  FullyConstrained = true
  MapMode = 5
  Support = -> [XY_Plane009]
  sketch-geometry (1):
    g0: Circle CenterX=0 CenterY=0 CenterZ=0 NormalX=0 NormalY=0 NormalZ=1 AngleXU=0 Radius=8.5
  constraints (2):
    c: Coincident(g0,g-1)
    c: Radius(g0) = 8.5
FEATURE [PartDesign::Pad] Pad013
  Direction = (1,1,1)
  Length = 65
  Length2 = 100
  Profile = -> Sketch020
  Type = 0
FEATURE [Sketcher::SketchObject] Sketch022
  FullyConstrained = true
  MapMode = 5
  Placement = pos=(0,0,65) rot=(0,0,1;0rad)
  Support = -> [Pad013]
  sketch-geometry (1):
    g0: Circle CenterX=0 CenterY=0 CenterZ=0 NormalX=0 NormalY=0 NormalZ=1 AngleXU=0 Radius=7.5
  constraints (2):
    c: Coincident(g0,g-1)
    c: Radius(g0) = 7.5
FEATURE [PartDesign::Pocket] Pocket001
  BaseFeature = -> Pad013
  Length = 85
  Length2 = 100
  Profile = -> Sketch022
  Type = 0
FEATURE [PartDesign::Body] Body009  label="Motor Support (2)"
  Group = -> [Sketch020,Pad013,Sketch022,Pocket001]
  Origin = -> Origin009
  Placement = pos=(-267,14.5,-82) rot=(0,0,1;0rad)
  Tip = -> Pocket001
FEATURE [Sketcher::SketchObject] Sketch024
  FullyConstrained = true
  MapMode = 5
  Support = -> [XY_Plane010]
  sketch-geometry (1):
    g0: Circle CenterX=0 CenterY=0 CenterZ=0 NormalX=0 NormalY=0 NormalZ=1 AngleXU=0 Radius=8.5
  constraints (2):
    c: Coincident(g0,g-1)
    c: Radius(g0) = 8.5
FEATURE [PartDesign::Pad] Pad014
  Direction = (1,1,1)
  Length = 65
  Length2 = 100
  Profile = -> Sketch024
  Type = 0
FEATURE [Sketcher::SketchObject] Sketch023
  FullyConstrained = true
  MapMode = 5
  Placement = pos=(0,0,65) rot=(0,0,1;0rad)
  Support = -> [Pad014]
  sketch-geometry (1):
    g0: Circle CenterX=0 CenterY=0 CenterZ=0 NormalX=0 NormalY=0 NormalZ=1 AngleXU=0 Radius=7.5
  constraints (2):
    c: Coincident(g0,g-1)
    c: Radius(g0) = 7.5
FEATURE [PartDesign::Pocket] Pocket002
  BaseFeature = -> Pad014
  Length = 85
  Length2 = 100
  Profile = -> Sketch023
  Type = 0
FEATURE [PartDesign::Body] Body010  label="Motor Support (1)"
  Group = -> [Sketch024,Pad014,Sketch023,Pocket002]
  Origin = -> Origin010
  Placement = pos=(-267,-6.5,-82) rot=(0,0,1;0rad)
  Tip = -> Pocket002
